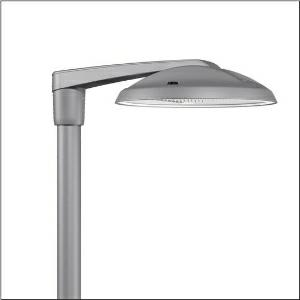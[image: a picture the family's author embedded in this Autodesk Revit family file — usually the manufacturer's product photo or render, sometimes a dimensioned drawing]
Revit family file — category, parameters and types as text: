
# Revit family: dl_r__50_mini___st1_0a_5xa248d33s08me_5901
name_source: partatom
category: Lighting Fixtures
units: mm (PartAtom-declared; Revit-internal decimal feet)

## family parameters
Cut with Voids When Loaded = No
Host = Face
Light Source = No
Part Type = Normal
Room Calculation Point = No
Round Connector Dimension = Use Diameter
Shared = No

## types (1)
- --- (1 x LED, 15380 lm, 110.3 W, 3000K)
    Apparent Load = 110 VA
    CIE Flux Codes = 37 72 97 100 100
    Color Rendering = 70
    Color Temperature = 3000K
    Default Elevation = 1800 mm
    Description = DL® 50 mini, mast luminaire, primary light control with lens, of PMMA, primary optical cover: cover, of toughened safety glass, transparent, light distribution: ST1.0a, light emission: direct distribution, primary light characteristic: asymmetric, installation type: post-top, side-entry, LED, High Power LED, rated luminous flux: 15.380lm, luminous efficacy: 139lm/W, light colour: 730, colour temperature: 3000K, control gear: D4i, control: overheat protection, constant luminous flux control, time-dependent luminous flux control, flexible luminous flux parameterisation, mains connection: 230..240V, AC, 50/60Hz, connection cable pre-assembled, cable length: 10,5m, start of lifetime: 110W, end of service life: 116W, reduction: 49W, luminaire housing, of diecast aluminium, powder-coated, Siteco® metallic grey (DB 702S), inclination adjustable: 0°, 5°, 10° (post-top) | 0°, -5°, -10°, -15° (side-entry), please order mast post-top element or mast side-entry element separately, diameter: 500mm, height: 115mm, post-top: for spigot size d x l = 76 x 100mm; with reducer (optional accessory) 60 x 100mm | side-entry: for spigot size d x l = 60 x 100mm; with reducer (optional accessory) 42 x 100mm, mounting height: 4..6m, Smart Interface above, protection rating (complete): IP66, insulation class (complete): insulation class II (safety insulation), certification: CE, ENEC, ENEC+, VDE, impact resistance: IK08, permissible operating ambient temperature for outdoor applications: -25..+40°C, standard-compliant lighting for roads and squares, packaging unit: 1 piece

Light Distribution: ST1.0a
    Height = 115 mm
    Lamp = 1 x LED
    Lamp Light Flux = 15380 lm
    Lamp Power = 110.3 W
    Lamp count = 1
    Length = 500 mm
    Luminous efficacy = 139 lm/W
    Manufacturer = Siteco
    ModVariant = No
    Model = 5XA248D33S08ME
    Number of Poles = 1
    OnlyDefault = Yes
    Power Factor = 1
    Product Name = DL® 50 mini | ST1.0a
    Product group = mast luminaire | pylon top
    ProductGroupID = 6100
    Protection Class = Protection class II
    Protection Degree = IP 66
    RLX_Detail_Level = 1
    RLX_Emergency_Light_Flux = 0 lm
    RLX_Emergency_Type = 0
    RLX_Emergency_Type_DB = No
    RlxData = <blob elided: 106161 chars, md5=1028b83f>
    Socket = socket
    Standby Power = 0 W
    System Light Flux = 15380 lm
    System Power = 110 W
    Type Comments = factory setting: luminous flux: 100 % | dim-lin: 254 | 565 mA
    Type Image = l_1251788.jpg
    URL = http://relux.com
    VarID = @adj_065218
    Voltage = 0 V
    Weight = 0.00 kg
    Width = 0 mm  [stored 0 ft]

note: [stored X ft] marks values corroborated as IEEE doubles in the binary element streams (Revit-internal decimal feet)

## geometry (parser evidence)
native form markers: Blend x4, Sweep x9
no freeform markers — native parametric forms only
